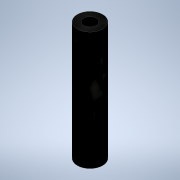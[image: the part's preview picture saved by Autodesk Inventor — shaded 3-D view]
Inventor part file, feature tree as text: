
AUTODESK INVENTOR PART (.ipt)
format: ipt  version: 2020.2 (Build 242310000, 310)  size: 91,136 bytes
history: native  units: mm
features: other x1, extrude x1, sketch x1
ambient origin geometry x8: Origin, YZ Plane, XZ Plane, XY Plane, X Axis, Y Axis, Z Axis, Center Point
bodies: Body1 (feature_tree)
feature tree (3):
  other  "ソリッド1"
  extrude  "押し出し1"  Depth=6.0mm
  sketch  "スケッチ1"
